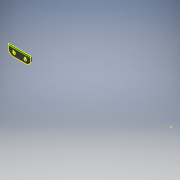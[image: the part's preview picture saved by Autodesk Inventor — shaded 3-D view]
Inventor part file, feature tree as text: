
AUTODESK INVENTOR PART (.ipt)
format: ipt  version: 2019.3 (Build 233278000, 278)  size: 145,920 bytes
history: native  units: mm
features: other x6, extrude x2, sketch x1, projected_geometry x1
ambient origin geometry x8: Origin, YZ Plane, XZ Plane, XY Plane, X Axis, Y Axis, Z Axis, Center Point
bodies: Body1 (feature_tree), Body2 (feature_tree), Body3 (feature_tree)
feature tree (10):
  other  "ChainGuideTab.ipt"
  sketch  "Sketch1"  dims[d0=10.0mm d1=1.5mm d2=0.0mm d3=2.0mm d4=0.0mm]
  extrude  "Extrusion1"  Depth=1.5mm TaperAngle=0.0deg
  extrude  "Extrusion2"  Depth=2.0mm TaperAngle=0.0deg
  other  "Solid1::ChainGuideTab.ipt"
  other  "TaggingFeature1"
  projected_geometry  "Projected Loop1"
  other  "ChainGuideSpacer1.5mm"
  other  "ChainGuideSpacer2mm"
  other  "ChainGuideSpacer4mm"
